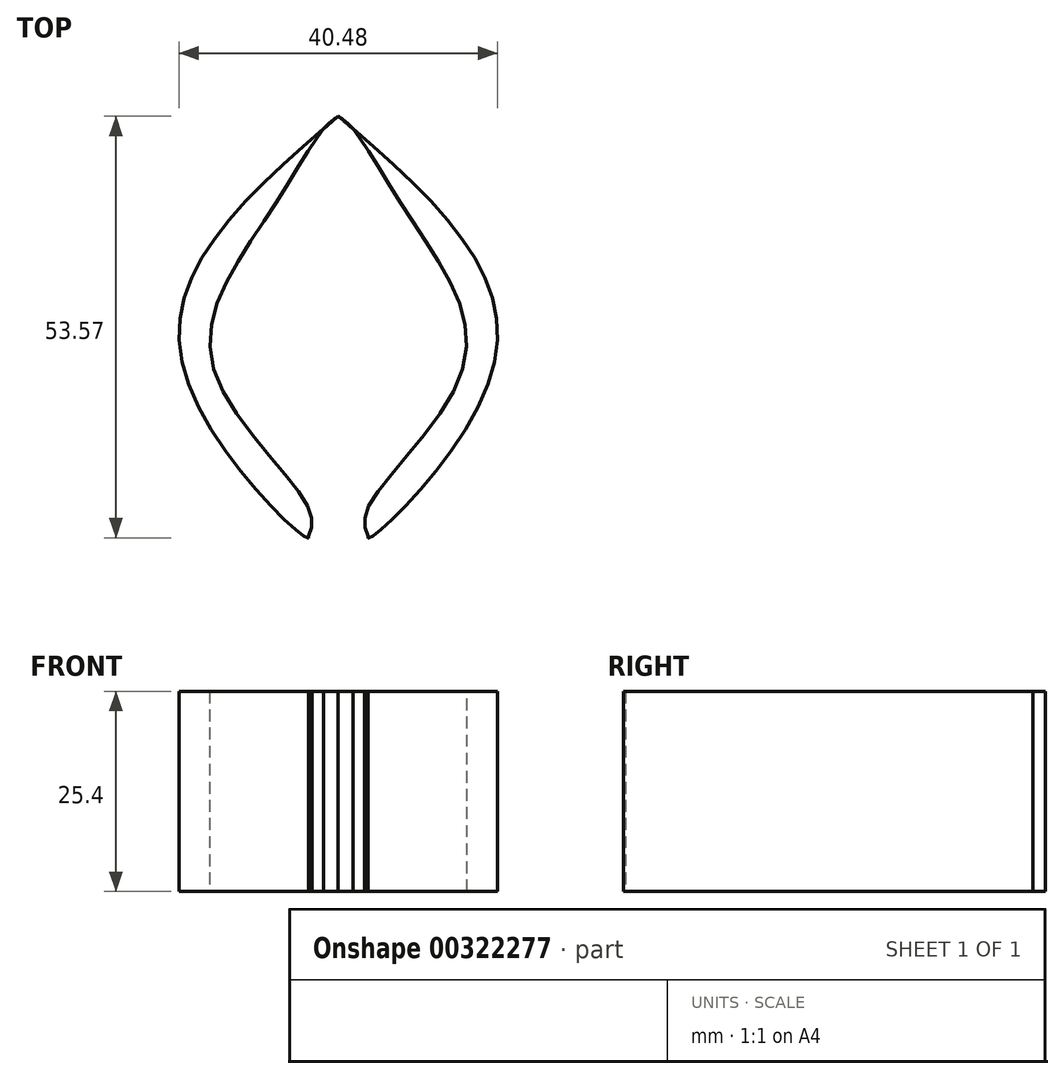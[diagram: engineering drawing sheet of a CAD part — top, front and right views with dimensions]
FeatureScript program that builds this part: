
annotation { "Feature Type Name" : "Feature", "Feature Type Description" : "" }
export const myFeature = defineFeature(function(context is Context, id is Id, definition is map)
    precondition{}
    {
        {
            var Q0;
            Q0=qCreatedBy(makeId("Top.planeOp"),FACE);
            var sketch = newSketch(context, id + "F0", { "sketchPlane" : qUnion([Q0])});
            skFitSpline(sketch, "E0", {"points": [v(0, 0) * mm, v(-19.84, -31.33) * mm, v(-3.84, -53.57) * mm, v(-3.77, -53.24) * mm], "startDerivative": vector(-66.05, -56.68) * mm, "endDerivative": vector(-1.5, 9.73) * mm});
            skFitSpline(sketch, "E1.MirrorCS", {"points": [v(0, 0) * mm, v(19.84, -31.33) * mm, v(3.84, -53.57) * mm, v(3.77, -53.24) * mm], "startDerivative": vector(66.05, -56.68) * mm, "endDerivative": vector(1.5, 9.73) * mm});
            skFitSpline(sketch, "E2", {"points": [v(3.84, -53.57) * mm, v(3.77, -49.74) * mm, v(16.02, -31.33) * mm, v(8.92, -12.56) * mm, v(1.85, -1.6) * mm, v(0, 0) * mm], "startDerivative": vector(-10.5, 27.02) * mm, "endDerivative": vector(-17.78, 12) * mm});
            skFitSpline(sketch, "E3.MirrorCS", {"points": [v(-3.84, -53.57) * mm, v(-3.77, -49.74) * mm, v(-16.02, -31.33) * mm, v(-8.92, -12.56) * mm, v(-1.85, -1.6) * mm, v(0, 0) * mm], "startDerivative": vector(10.5, 27.02) * mm, "endDerivative": vector(17.78, 12) * mm});
            skSolve(sketch);
        }
        {
            var Q0;
            Q0 = qSketchRegion(id + "F0", true);
            extrude(context, id + "F1", {"entities" : qUnion([Q0]), "depth" : 25.4 * mm});
        }
    });
